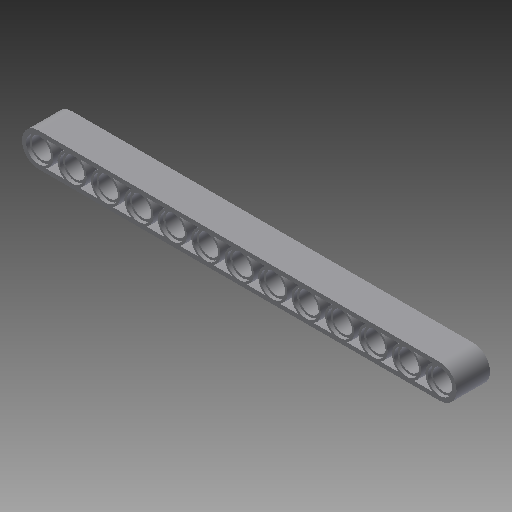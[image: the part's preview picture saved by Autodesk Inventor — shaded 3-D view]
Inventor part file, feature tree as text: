
AUTODESK INVENTOR PART (.ipt)
format: ipt  version: 2018 (Build 220112000, 112)  size: 287,232 bytes
history: native  units: mm
features: extrude x5, sketch x5
ambient origin geometry x8: Origin, YZ Plane, XZ Plane, XY Plane, X Axis, Y Axis, Z Axis, Center Point
bodies: Solid1 (feature_tree)
feature tree (10):
  extrude  "Extrusion1"  Depth=4.0mm
  extrude  "Extrusion22"  TaperAngle=0.0deg  [1 undecoded]
  extrude  "Extrusion23"  TaperAngle=180.0deg  [1 undecoded]
  extrude  "Extrusion24"  Depth=8.0mm TaperAngle=0.0deg
  extrude  "Extrusion25"  Depth=0.8mm
  sketch  "Sketch2"  dims[d0=4.0mm d1=4.0mm]
  sketch  "Sketch23"  dims[d2=96.0mm d3=0.0mm]
  sketch  "Sketch24"  dims[d4=48.0mm d9=180.0deg]
  sketch  "Sketch25"  dims[d10=0.0mm d12=8.0mm d13=0.0mm]
  sketch  "Sketch26"  dims[d225=96.0mm d226=5.0mm d227=10.0mm d229=10.0mm d230=130.0mm d232=8.0mm d234=10.0mm d235=0.0mm d236=6.0mm d237=10.0mm d239=10.0mm d240=130.0mm d242=8.0mm d244=0.8mm d245=0.0mm d246=6.0mm d247=10.0mm d249=10.0mm d250=130.0mm d252=8.0mm d254=0.8mm d255=0.0mm d257=7.0mm d258=7.0mm d259=10.0mm d261=10.0mm d262=120.0mm d264=8.0mm d266=0.8mm d267=0.0mm]
note: 2 required parameter values undecoded (feature->parameter linkage not recoverable at this tier; creation-order binding heuristic only, values carry confidence <= 0.55)
